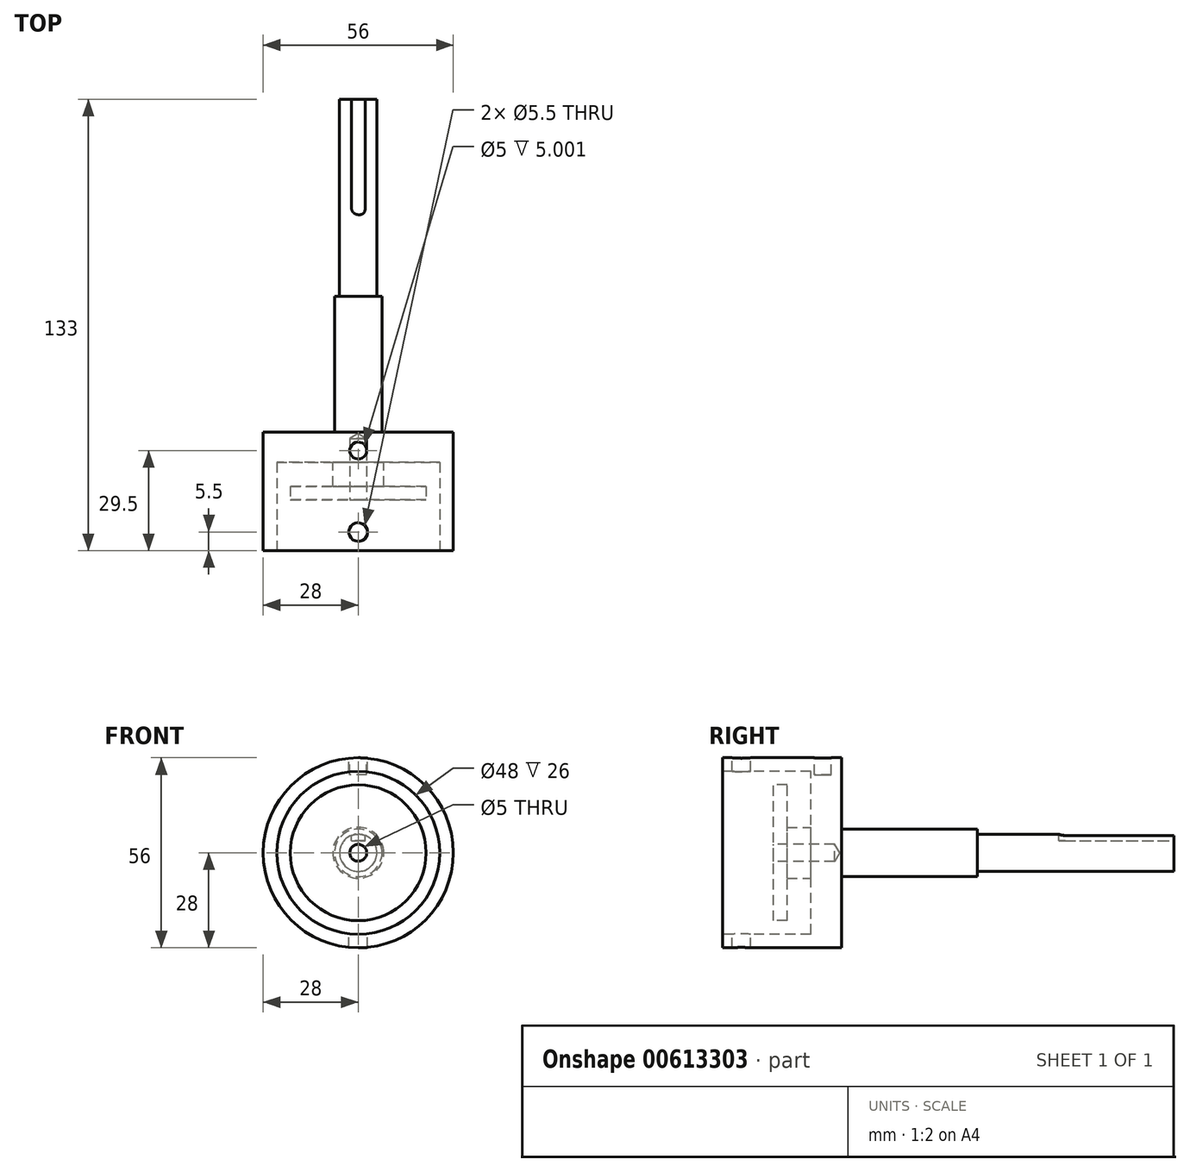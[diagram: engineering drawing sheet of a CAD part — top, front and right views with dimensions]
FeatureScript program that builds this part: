
annotation { "Feature Type Name" : "Feature", "Feature Type Description" : "" }
export const myFeature = defineFeature(function(context is Context, id is Id, definition is map)
    precondition{}
    {
        {
            var Q0;
            Q0=qCreatedBy(makeId("Right.planeOp"),FACE);
            var sketch = newSketch(context, id + "F0", { "sketchPlane" : qUnion([Q0])});
            skLineSegment(sketch, "E0", {"start": v(0, 0) * mm, "end": v(133, 0) * mm});
            skLineSegment(sketch, "E1", {"start": v(0, 0) * mm, "end": v(0, 28) * mm});
            skLineSegment(sketch, "E2", {"start": v(0, 28) * mm, "end": v(35, 28) * mm});
            skLineSegment(sketch, "E3", {"start": v(35, 28) * mm, "end": v(35, 7) * mm});
            skLineSegment(sketch, "E4", {"start": v(35, 7) * mm, "end": v(75, 7) * mm});
            skLineSegment(sketch, "E5", {"start": v(75, 7) * mm, "end": v(75, 5.5) * mm});
            skLineSegment(sketch, "E6", {"start": v(75, 5.5) * mm, "end": v(133, 5.5) * mm});
            skLineSegment(sketch, "E7", {"start": v(133, 5.5) * mm, "end": v(133, 0) * mm});
            skSolve(sketch);
        }
        {
            var Q0;
            Q0 = qSketchRegion(id + "F0", true);
            var Q1;
            Q1=sQuery(id+"F0.wireOp",EDGE,"E0");
            revolve(context, id + "F1", {"entities" : qUnion([Q0]), "axis" : qUnion([Q1]), "revolveType" : RevolveType.FULL});
        }
        {
            var Q0;
            Q0=qCreatedBy(makeId("Top.planeOp"),FACE);
            cPlane(context, id + "F2", {"entities" : qUnion([Q0]), "cplaneType" : CPlaneType.OFFSET, "offset" : 5.5 * mm, "width" : 150 * mm, "height" : 150 * mm});
        }
        {
            var Q0;
            Q0=qCreatedBy(id+"F2.planeOp",FACE);
            var sketch = newSketch(context, id + "F3", { "sketchPlane" : qUnion([Q0])});
            skLineSegment(sketch, "E8.bottom", {"start": v(0.5, 99) * mm, "end": v(0, 99) * mm});
            skLineSegment(sketch, "E8.top", {"start": v(2, 133) * mm, "end": v(-2, 133) * mm});
            skLineSegment(sketch, "E8.left", {"start": v(2, 100.5) * mm, "end": v(2, 133) * mm});
            skLineSegment(sketch, "E8.right", {"start": v(-2, 101) * mm, "end": v(-2, 133) * mm});
            skPoint(sketch, "E9.visualSharp", {"position": v(-2, 99) * mm});
            skArc(sketch, "E9.filletArc", {"start": v(-2, 101) * mm, "mid": v(-1.41, 99.59) * mm, "end": v(0, 99) * mm});
            skPoint(sketch, "E10.visualSharp", {"position": v(2, 99) * mm});
            skArc(sketch, "E10.filletArc", {"start": v(0.5, 99) * mm, "mid": v(1.56, 99.44) * mm, "end": v(2, 100.5) * mm});
            skSolve(sketch);
        }
        {
            var Q0;
            Q0 = qSketchRegion(id + "F3", true);
            extrude(context, id + "F4", {"entities" : qUnion([Q0]), "operationType" : NewBodyOperationType.REMOVE, "oppositeDirection" : true, "depth" : 2 * mm, "offsetDistance" : 25 * mm});
        }
        {
            var Q0;
            Q0=makeQuery(id+"F1.opRevolve","SWEPT_FACE",FACE,{"disambiguationData":[OSD([sQuery(id+"F0.wireOp",EDGE,"E1")])]});
            var sketch = newSketch(context, id + "F5", { "sketchPlane" : qUnion([Q0])});
            skCircle(sketch, "E11", {"center": v(0, 0) * mm, "radius": 24 * mm});
            skSolve(sketch);
        }
        {
            var Q0;
            Q0 = qSketchRegion(id + "F5", true);
            extrude(context, id + "F6", {"entities" : qUnion([Q0]), "operationType" : NewBodyOperationType.REMOVE, "oppositeDirection" : true, "depth" : 26 * mm, "offsetDistance" : 25 * mm});
        }
        {
            var Q0;
            Q0=makeQuery(id+"F6.boolean.opBoolean","COPY",FACE,{"derivedFrom":makeQuery(id+"F6.opExtrude","CAP_FACE",FACE,{"disambiguationData":[OSD([sQuery(id+"F5.wireOp",EDGE,"E11")])],"isStart":false})});
            var sketch = newSketch(context, id + "F7", { "sketchPlane" : qUnion([Q0])});
            skCircle(sketch, "E12", {"center": v(0, 0) * mm, "radius": 7.5 * mm});
            skSolve(sketch);
        }
        {
            var Q0;
            Q0 = qSketchRegion(id + "F7", true);
            extrude(context, id + "F8", {"entities" : qUnion([Q0]), "operationType" : NewBodyOperationType.ADD, "depth" : 11 * mm, "offsetDistance" : 25 * mm});
        }
        {
            var Q0;
            Q0=makeQuery(id+"F8.opExtrude","CAP_FACE",FACE,{"disambiguationData":[OSD([sQuery(id+"F7.wireOp",EDGE,"E12")])],"isStart":false});
            var sketch = newSketch(context, id + "F9", { "sketchPlane" : qUnion([Q0])});
            skCircle(sketch, "E13", {"center": v(0, 0) * mm, "radius": 20 * mm});
            skSolve(sketch);
        }
        {
            var Q0;
            Q0 = qSketchRegion(id + "F9", true);
            extrude(context, id + "F10", {"entities" : qUnion([Q0]), "operationType" : NewBodyOperationType.ADD, "oppositeDirection" : true, "depth" : 4 * mm, "offsetDistance" : 25 * mm});
        }
        {
            var Q0;
            Q0=qCreatedBy(makeId("Top.planeOp"),FACE);
            cPlane(context, id + "F11", {"entities" : qUnion([Q0]), "cplaneType" : CPlaneType.OFFSET, "offset" : 28 * mm, "width" : 150 * mm, "height" : 150 * mm});
        }
        {
            var Q0;
            Q0=qCreatedBy(id+"F11.planeOp",FACE);
            var sketch = newSketch(context, id + "F12", { "sketchPlane" : qUnion([Q0])});
            skPoint(sketch, "E14", {"position": v(0, 5.5) * mm});
            skSolve(sketch);
        }
        {
            var Q0;
            Q0=sQuery(id+"F12.wireOp",VERTEX,"E14");
            var Q1;
            Q1=makeQuery(id+"F1.opRevolve","SWEPT_BODY",BODY,{"disambiguationData":[OSD([sQuery(id+"F0.wireOp",EDGE,"E0"),sQuery(id+"F0.wireOp",EDGE,"E1"),sQuery(id+"F0.wireOp",EDGE,"E2"),sQuery(id+"F0.wireOp",EDGE,"E3"),sQuery(id+"F0.wireOp",EDGE,"E4"),sQuery(id+"F0.wireOp",EDGE,"E5"),sQuery(id+"F0.wireOp",EDGE,"E6"),sQuery(id+"F0.wireOp",EDGE,"E7")])]});
            hole(context, id + "F13", {"style" : HoleStyle.SIMPLE, "endStyle" : HoleEndStyle.THROUGH, "standardTappedOrClearance" : lookupTablePath({ "standard" : "ISO", "fit" : "Normal", "size" : "M5", "type" : "Clearance" }), "standardBlindInLast" : lookupTablePath({ "fit" : "Standard", "standard" : "ISO", "size" : "M5", "type" : "Clearance" }), "holeDiameter" : 5.5 * mm, "majorDiameter" : 5 * mm, "isTappedThrough" : true, "tappedDepth" : 12 * mm, "tapClearance" : 3, "startFromSketch" : true, "locations" : qUnion([Q0]), "scope" : qUnion([Q1])});
        }
        {
            var Q0;
            Q0=qCreatedBy(id+"F11.planeOp",FACE);
            var sketch = newSketch(context, id + "F14", { "sketchPlane" : qUnion([Q0])});
            skCircle(sketch, "E15", {"center": v(0, 29.5) * mm, "radius": 2.5 * mm});
            skSolve(sketch);
        }
        {
            var Q0;
            Q0 = qSketchRegion(id + "F14", true);
            extrude(context, id + "F15", {"entities" : qUnion([Q0]), "operationType" : NewBodyOperationType.REMOVE, "oppositeDirection" : true, "depth" : 5 * mm, "offsetDistance" : 25 * mm});
        }
        {
            var Q0;
            Q0=makeQuery(id+"F10.boolean.opBoolean","MERGE",FACE,{"derivedFrom":[makeQuery(id+"F8.opExtrude","CAP_FACE",FACE,{"disambiguationData":[OSD([sQuery(id+"F7.wireOp",EDGE,"E12")])],"isStart":false}),makeQuery(id+"F10.opExtrude","CAP_FACE",FACE,{"disambiguationData":[OSD([sQuery(id+"F9.wireOp",EDGE,"E13")])],"isStart":true})]});
            var sketch = newSketch(context, id + "F16", { "sketchPlane" : qUnion([Q0])});
            skPoint(sketch, "E16", {"position": v(0, 0) * mm});
            skSolve(sketch);
        }
        {
            var Q0;
            Q0=sQuery(id+"F16.wireOp",VERTEX,"E16");
            var Q1;
            Q1=makeQuery(id+"F1.opRevolve","SWEPT_BODY",BODY,{"disambiguationData":[OSD([sQuery(id+"F0.wireOp",EDGE,"E0"),sQuery(id+"F0.wireOp",EDGE,"E1"),sQuery(id+"F0.wireOp",EDGE,"E2"),sQuery(id+"F0.wireOp",EDGE,"E3"),sQuery(id+"F0.wireOp",EDGE,"E4"),sQuery(id+"F0.wireOp",EDGE,"E5"),sQuery(id+"F0.wireOp",EDGE,"E6"),sQuery(id+"F0.wireOp",EDGE,"E7")])]});
            hole(context, id + "F17", {"style" : HoleStyle.SIMPLE, "endStyle" : HoleEndStyle.BLIND, "holeDiameter" : 5 * mm, "majorDiameter" : 5 * mm, "holeDepth" : 18 * mm, "isTappedThrough" : true, "tappedDepth" : 12 * mm, "tapClearance" : 3, "startFromSketch" : true, "locations" : qUnion([Q0]), "scope" : qUnion([Q1])});
        }
    });
